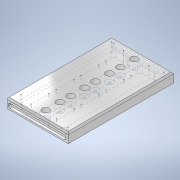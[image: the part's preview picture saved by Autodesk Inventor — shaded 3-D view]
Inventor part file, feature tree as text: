
AUTODESK INVENTOR PART (.ipt)
format: ipt  version: 2022 (Build 260153000, 153)  size: 271,360 bytes
history: native  units: in
note: dims shown in document units (in); Inventor stores cm internally (conversion verified against a paired STEP export)
features: sketch x7, extrude x4, hole x3, chamfer x2
ambient origin geometry x8: Origin, YZ Plane, XZ Plane, XY Plane, X Axis, Y Axis, Z Axis, Center Point
bodies: Solid1 (feature_tree)
feature tree (16):
  extrude  "Extrusion1"  Depth=8.5in
  hole  "Hole2"  [1 undecoded]
  hole  "Hole3"  [1 undecoded]
  hole  "Hole4"  [1 undecoded]
  chamfer  "Chamfer1"  Distance=0.4075in
  chamfer  "Chamfer2"  Distance=0.4075in
  extrude  "Extrusion3"  Depth=0.1875in
  extrude  "Extrusion4"  Depth=0.1875in
  extrude  "Extrusion5"  Depth=0.1875in
  sketch  "Sketch1"  dims[d0=5.0in d1=8.5in]
  sketch  "Sketch4"  dims[d2=0.75in d3=0.0in d14=0.687in]
  sketch  "Sketch5"  dims[d15=1.8135in d16=1.5748in d18=2.0in d19=0.3937in d21=1.0in]
  sketch  "Sketch6"  dims[d23=0.156in d24=0.75in d25=0.55in d26=0.6in d27=0.5635in d28=1.0in d29=0.8108in d31=0.7894in]
  sketch  "Sketch7"  dims[d32=0.4075in]
  sketch  "Sketch8"  dims[d33=0.4075in]
  sketch  "Sketch9"  dims[d34=0.4075in d35=0.4075in d36=0.4075in d37=0.4075in d38=0.4075in d39=0.0402in d40=0.094in d41=0.119in d42=0.0787in d43=0.5635in d44=0.315in d45=0.8108in d46=1.4213in d47=2.0276in d48=0.5394in d49=1.4862in d50=1.5748in d52=2.0in d53=0.3937in d55=0.3937in d57=0.0465in d58=0.12in d59=0.1575in d60=0.0787in d61=90.0deg d62=0.315in d63=0.8108in d64=0.125in d65=0.0787in d66=45.0deg d67=0.125in d68=0.0787in d69=45.0deg d70=0.75in d71=0.375in d72=0.625in d73=0.3937in d74=0.1969in d75=0.5in d76=0.0in d77=0.35in d78=0.1875in d79=0.1875in d80=0.125in d81=0.1875in d82=0.0in d83=0.125in d84=0.35in d88=0.125in d89=0.125in d90=0.1875in d91=0.1875in d92=0.0in]
note: 3 required parameter values undecoded (feature->parameter linkage not recoverable at this tier; creation-order binding heuristic only, values carry confidence <= 0.55)
